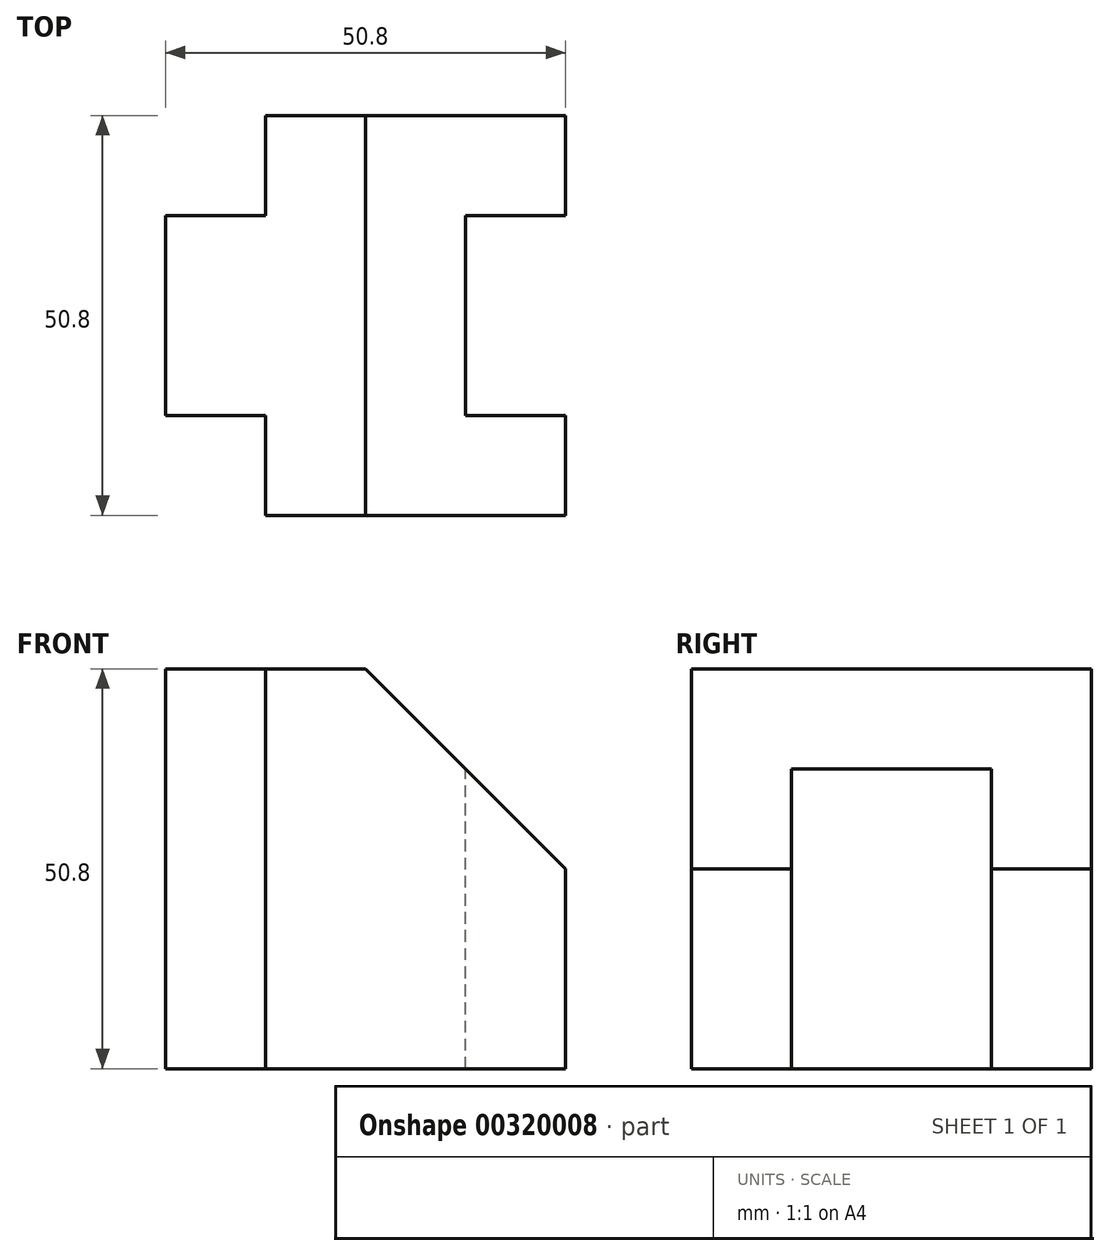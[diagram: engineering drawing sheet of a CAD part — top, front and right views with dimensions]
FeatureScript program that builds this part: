
annotation { "Feature Type Name" : "Feature", "Feature Type Description" : "" }
export const myFeature = defineFeature(function(context is Context, id is Id, definition is map)
    precondition{}
    {
        {
            var Q0;
            Q0=qCreatedBy(makeId("Front.planeOp"),FACE);
            var sketch = newSketch(context, id + "F0", { "sketchPlane" : qUnion([Q0])});
            skLineSegment(sketch, "E0.bottom", {"start": v(0, 0) * mm, "end": v(50.8, 0) * mm});
            skLineSegment(sketch, "E0.top", {"start": v(0, 50.8) * mm, "end": v(50.8, 50.8) * mm});
            skLineSegment(sketch, "E0.left", {"start": v(0, 0) * mm, "end": v(0, 50.8) * mm});
            skLineSegment(sketch, "E0.right", {"start": v(50.8, 0) * mm, "end": v(50.8, 50.8) * mm});
            skSolve(sketch);
        }
        {
            var Q0;
            Q0 = qSketchRegion(id + "F0", true);
            extrude(context, id + "F1", {"entities" : qUnion([Q0]), "oppositeDirection" : true, "depth" : 50.8 * mm});
        }
        {
            var Q0;
            Q0=makeQuery(id+"F1.opExtrude","SWEPT_FACE",FACE,{"disambiguationData":[OSD([sQuery(id+"F0.wireOp",EDGE,"E0.top")])]});
            var sketch = newSketch(context, id + "F2", { "sketchPlane" : qUnion([Q0])});
            skLineSegment(sketch, "E1", {"start": v(0, 38.1) * mm, "end": v(12.7, 38.1) * mm});
            skLineSegment(sketch, "E2", {"start": v(12.7, 38.1) * mm, "end": v(12.7, 50.8) * mm});
            skLineSegment(sketch, "E3", {"start": v(0, 12.7) * mm, "end": v(12.7, 12.7) * mm});
            skLineSegment(sketch, "E4", {"start": v(12.7, 12.7) * mm, "end": v(12.7, 0) * mm});
            skLineSegment(sketch, "E5", {"start": v(50.8, 38.1) * mm, "end": v(38.1, 38.1) * mm});
            skLineSegment(sketch, "E6", {"start": v(38.1, 38.1) * mm, "end": v(38.1, 12.7) * mm});
            skLineSegment(sketch, "E7", {"start": v(38.1, 12.7) * mm, "end": v(50.8, 12.7) * mm});
            skSolve(sketch);
        }
        {
            var Q0;
            {var subQ0=sQuery(id+"F2.wireOp",EDGE,"E1");Q0=makeQuery(id+"F2.imprint","IMPRINT",FACE,{"disambiguationData":[TD([[makeQuery(id+"F2.imprint","IMPRINT",EDGE,{"derivedFrom":subQ0}),1.0]])]});}
            var Q1;
            {var subQ0=sQuery(id+"F2.wireOp",EDGE,"E3");Q1=makeQuery(id+"F2.imprint","IMPRINT",FACE,{"disambiguationData":[TD([[makeQuery(id+"F2.imprint","IMPRINT",EDGE,{"derivedFrom":subQ0}),-1.0]])]});}
            var Q2;
            {var subQ0=sQuery(id+"F2.wireOp",EDGE,"E5");Q2=makeQuery(id+"F2.imprint","IMPRINT",FACE,{"disambiguationData":[TD([[makeQuery(id+"F2.imprint","IMPRINT",EDGE,{"derivedFrom":subQ0}),1.0]])]});}
            extrude(context, id + "F3", {"entities" : qUnion([Q0, Q1, Q2]), "operationType" : NewBodyOperationType.REMOVE, "oppositeDirection" : true, "depth" : 76.2 * mm});
        }
        {
            var Q0;
            Q0=makeQuery(id+"F1.opExtrude","CAP_FACE",FACE,{"disambiguationData":[OSD([sQuery(id+"F0.wireOp",EDGE,"E0.bottom"),sQuery(id+"F0.wireOp",EDGE,"E0.top"),sQuery(id+"F0.wireOp",EDGE,"E0.left"),sQuery(id+"F0.wireOp",EDGE,"E0.right")])],"isStart":true});
            var sketch = newSketch(context, id + "F4", { "sketchPlane" : qUnion([Q0])});
            skLineSegment(sketch, "E8", {"start": v(25.4, 50.8) * mm, "end": v(50.8, 25.4) * mm});
            skSolve(sketch);
        }
        {
            var Q0;
            {var subQ0=sQuery(id+"F4.wireOp",EDGE,"E8");Q0=makeQuery(id+"F4.imprint","IMPRINT",FACE,{"disambiguationData":[TD([[makeQuery(id+"F4.imprint","IMPRINT",EDGE,{"derivedFrom":subQ0}),1.0]])]});}
            extrude(context, id + "F5", {"entities" : qUnion([Q0]), "operationType" : NewBodyOperationType.REMOVE, "oppositeDirection" : true, "depth" : 101.6 * mm});
        }
    });
